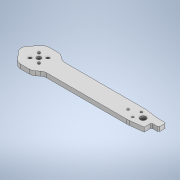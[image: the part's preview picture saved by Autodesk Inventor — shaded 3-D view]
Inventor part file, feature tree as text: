
AUTODESK INVENTOR PART (.ipt)
format: ipt  version: 2020 (Build 240168000, 168)  size: 167,424 bytes
history: native  units: mm
features: extrude x1, sketch x1
ambient origin geometry x8: Origin, YZ Plane, XZ Plane, XY Plane, X Axis, Y Axis, Z Axis, Center Point
bodies: Solid1 (feature_tree)
feature tree (2):
  extrude  "Extrusion1"  [1 undecoded]
  sketch  "Sketch1"  dims[d0=6.0mm d1=0.0mm]
note: 1 required parameter value undecoded (feature->parameter linkage not recoverable at this tier; creation-order binding heuristic only, values carry confidence <= 0.55)
